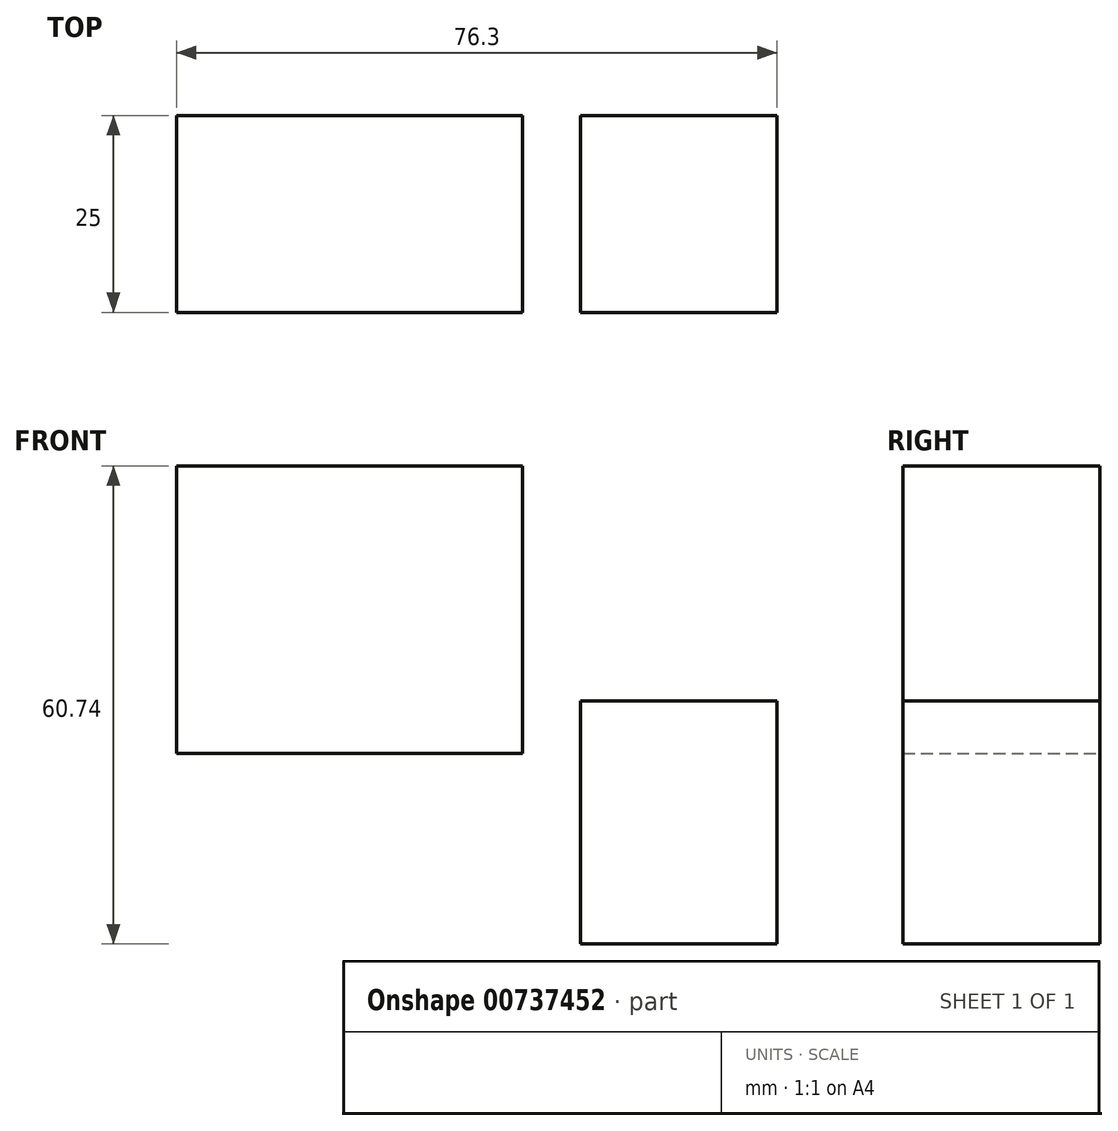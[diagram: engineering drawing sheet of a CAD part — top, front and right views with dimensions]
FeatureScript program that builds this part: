
annotation { "Feature Type Name" : "Feature", "Feature Type Description" : "" }
export const myFeature = defineFeature(function(context is Context, id is Id, definition is map)
    precondition{}
    {
        {
            var Q0;
            Q0=qCreatedBy(makeId("Front.planeOp"),FACE);
            var sketch = newSketch(context, id + "F0", { "sketchPlane" : qUnion([Q0])});
            skLineSegment(sketch, "E0.bottom", {"start": v(-63.83, 8.77) * mm, "end": v(-19.88, 8.77) * mm});
            skLineSegment(sketch, "E0.top", {"start": v(-63.83, 45.31) * mm, "end": v(-19.88, 45.31) * mm});
            skLineSegment(sketch, "E0.left", {"start": v(-63.83, 8.77) * mm, "end": v(-63.83, 45.31) * mm});
            skLineSegment(sketch, "E0.right", {"start": v(-19.88, 8.77) * mm, "end": v(-19.88, 45.31) * mm});
            skPoint(sketch, "E0.middle", {"position": v(-41.86, 27.04) * mm});
            skLineSegment(sketch, "E1.bottom", {"start": v(-12.47, -15.43) * mm, "end": v(12.47, -15.43) * mm});
            skLineSegment(sketch, "E1.top", {"start": v(-12.47, 15.43) * mm, "end": v(12.47, 15.43) * mm});
            skLineSegment(sketch, "E1.left", {"start": v(-12.47, -15.43) * mm, "end": v(-12.47, 15.43) * mm});
            skLineSegment(sketch, "E1.right", {"start": v(12.47, -15.43) * mm, "end": v(12.47, 15.43) * mm});
            skPoint(sketch, "E1.middle", {"position": v(0, 0) * mm});
            skSolve(sketch);
        }
        {
            var Q0;
            Q0=makeQuery(id+"F0.imprint","IMPRINT",FACE,{"disambiguationData":[TD([[makeQuery(id+"F0.imprint","IMPRINT",EDGE,{"derivedFrom":sQuery(id+"F0.wireOp",EDGE,"E0.bottom")}),1.0]])]});
            var Q1;
            Q1=makeQuery(id+"F0.imprint","IMPRINT",FACE,{"disambiguationData":[TD([[makeQuery(id+"F0.imprint","IMPRINT",EDGE,{"derivedFrom":sQuery(id+"F0.wireOp",EDGE,"E1.bottom")}),1.0]])]});
            extrude(context, id + "F1", {"entities" : qUnion([Q0, Q1]), "depth" : 25 * mm, "offsetDistance" : 25 * mm});
        }
    });
